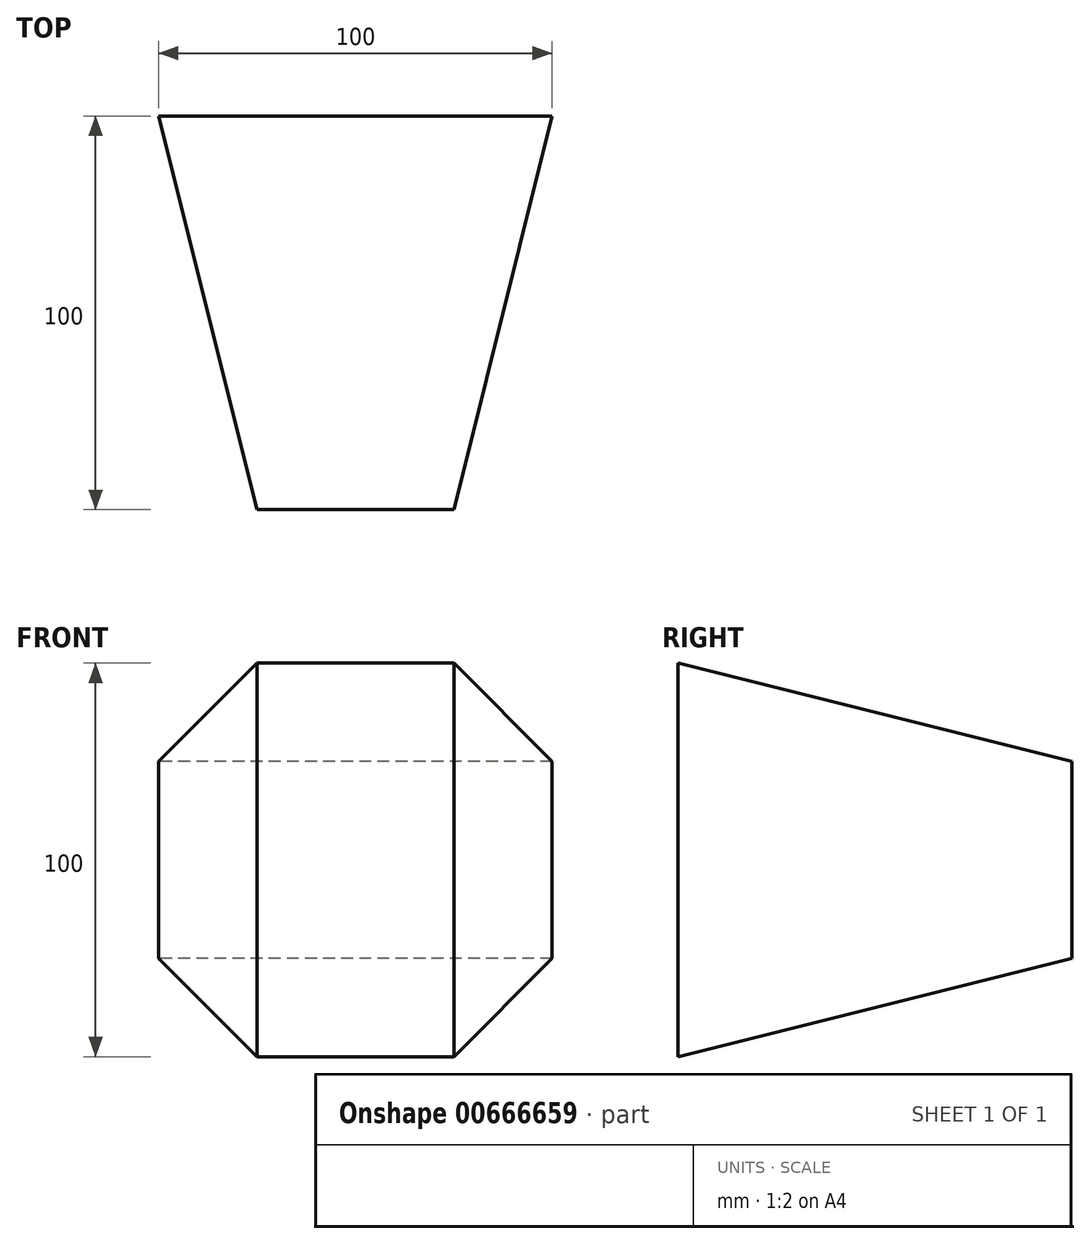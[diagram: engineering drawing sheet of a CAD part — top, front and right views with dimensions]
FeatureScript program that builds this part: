
annotation { "Feature Type Name" : "Feature", "Feature Type Description" : "" }
export const myFeature = defineFeature(function(context is Context, id is Id, definition is map)
    precondition{}
    {
        {
            var Q0;
            Q0=qCreatedBy(makeId("Front.planeOp"),FACE);
            var sketch = newSketch(context, id + "F0", { "sketchPlane" : qUnion([Q0])});
            skLineSegment(sketch, "E0.bottom", {"start": v(-25.4, 66.14) * mm, "end": v(24.6, 66.14) * mm});
            skLineSegment(sketch, "E0.top", {"start": v(-25.4, -33.86) * mm, "end": v(24.6, -33.86) * mm});
            skLineSegment(sketch, "E0.left", {"start": v(-25.4, 66.14) * mm, "end": v(-25.4, -33.86) * mm});
            skLineSegment(sketch, "E0.right", {"start": v(24.6, 66.14) * mm, "end": v(24.6, -33.86) * mm});
            skPoint(sketch, "E1", {"position": v(-25.4, 41.14) * mm});
            skPoint(sketch, "E2", {"position": v(24.6, 41.14) * mm});
            skPoint(sketch, "E3", {"position": v(24.6, -8.86) * mm});
            skPoint(sketch, "E4", {"position": v(-25.4, -8.86) * mm});
            skSolve(sketch);
        }
        {
            var Q0;
            Q0=qCreatedBy(makeId("Front.planeOp"),FACE);
            cPlane(context, id + "F1", {"entities" : qUnion([Q0]), "cplaneType" : CPlaneType.OFFSET, "offset" : 100 * mm, "oppositeDirection" : true, "width" : 150 * mm, "height" : 150 * mm});
        }
        {
            var Q0;
            Q0=qCreatedBy(id+"F1.planeOp",FACE);
            var sketch = newSketch(context, id + "F2", { "sketchPlane" : qUnion([Q0])});
            skLineSegment(sketch, "E5.bottom", {"start": v(49.6, 41.14) * mm, "end": v(-50.4, 41.14) * mm});
            skLineSegment(sketch, "E5.top", {"start": v(49.6, -8.86) * mm, "end": v(-50.4, -8.86) * mm});
            skLineSegment(sketch, "E5.left", {"start": v(49.6, 41.14) * mm, "end": v(49.6, -8.86) * mm});
            skLineSegment(sketch, "E5.right", {"start": v(-50.4, 41.14) * mm, "end": v(-50.4, -8.86) * mm});
            skSolve(sketch);
        }
        {
            var Q0;
            Q0=makeQuery(id+"F2.imprint","IMPRINT",FACE,{"disambiguationData":[TD([[makeQuery(id+"F2.imprint","IMPRINT",EDGE,{"derivedFrom":sQuery(id+"F2.wireOp",EDGE,"E5.bottom")}),1.0]])]});
            var Q1;
            Q1=makeQuery(id+"F0.imprint","IMPRINT",FACE,{"disambiguationData":[TD([[makeQuery(id+"F0.imprint","IMPRINT",EDGE,{"derivedFrom":sQuery(id+"F0.wireOp",EDGE,"E0.bottom")}),-1.0]])]});
            loft(context, id + "F3", {"sheetProfilesArray" : [{ "sheetProfileEntities" : qUnion([Q0]) }, { "sheetProfileEntities" : qUnion([Q1]) }]});
        }
    });
